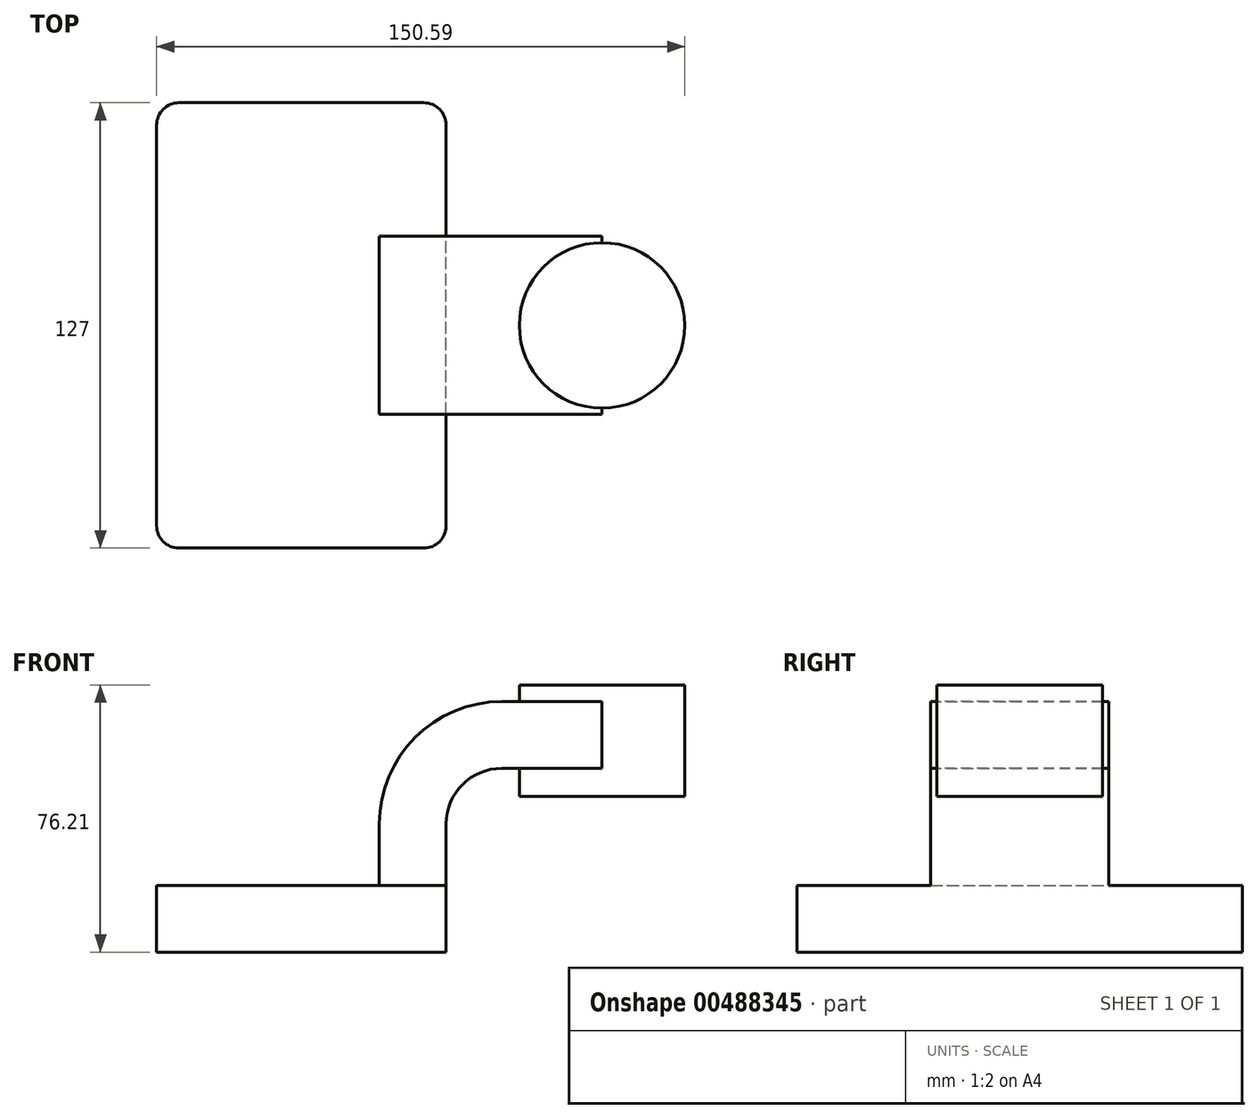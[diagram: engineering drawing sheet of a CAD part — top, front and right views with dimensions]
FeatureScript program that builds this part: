
annotation { "Feature Type Name" : "Feature", "Feature Type Description" : "" }
export const myFeature = defineFeature(function(context is Context, id is Id, definition is map)
    precondition{}
    {
        {
            var Q0;
            Q0=qCreatedBy(makeId("Front.planeOp"),FACE);
            var sketch = newSketch(context, id + "F0", { "sketchPlane" : qUnion([Q0])});
            skLineSegment(sketch, "E0.bottom", {"start": v(41.28, -9.52) * mm, "end": v(-41.28, -9.53) * mm});
            skLineSegment(sketch, "E0.top", {"start": v(41.27, 9.53) * mm, "end": v(-41.28, 9.52) * mm});
            skLineSegment(sketch, "E0.left", {"start": v(41.28, -9.52) * mm, "end": v(41.28, 9.53) * mm});
            skLineSegment(sketch, "E0.right", {"start": v(-41.28, -9.53) * mm, "end": v(-41.28, 9.52) * mm});
            skPoint(sketch, "E0.middle", {"position": v(0, 0) * mm});
            skLineSegment(sketch, "E1.bottom", {"start": v(109.32, 34.93) * mm, "end": v(58.52, 34.93) * mm});
            skLineSegment(sketch, "E1.top", {"start": v(109.32, 66.68) * mm, "end": v(58.52, 66.68) * mm});
            skLineSegment(sketch, "E1.left", {"start": v(109.32, 34.93) * mm, "end": v(109.32, 66.68) * mm});
            skLineSegment(sketch, "E1.right", {"start": v(58.52, 34.93) * mm, "end": v(58.52, 66.68) * mm});
            skPoint(sketch, "E1.middle", {"position": v(83.92, 50.8) * mm});
            skLineSegment(sketch, "E2", {"start": v(41.27, 9.53) * mm, "end": v(41.27, 27) * mm});
            skArc(sketch, "E3", {"start": v(41.28, 27) * mm, "mid": v(45.92, 38.23) * mm, "end": v(57.15, 42.88) * mm});
            skLineSegment(sketch, "E4", {"start": v(57.15, 42.88) * mm, "end": v(85.73, 42.88) * mm});
            skLineSegment(sketch, "E5.0", {"start": v(57.15, 61.93) * mm, "end": v(85.73, 61.93) * mm});
            skArc(sketch, "E5.1", {"start": v(22.23, 27) * mm, "mid": v(32.45, 51.7) * mm, "end": v(57.15, 61.93) * mm});
            skLineSegment(sketch, "E5.2", {"start": v(22.23, 9.53) * mm, "end": v(22.23, 27) * mm});
            skFitSpline(sketch, "E6", {"points": [v(-41.28, 9.52) * mm, v(57.15, 61.93) * mm], "startDerivative": vector(-7.2, 101.27) * mm, "endDerivative": vector(150.2, -4.26) * mm});
            skLineSegment(sketch, "E7", {"start": v(85.73, 34.93) * mm, "end": v(85.73, 66.68) * mm});
            skSolve(sketch);
        }
        {
            var Q0;
            Q0=makeQuery(id+"F0.imprint","IMPRINT",FACE,{"disambiguationData":[TD([[makeQuery(id+"F0.imprint","IMPRINT",EDGE,{"derivedFrom":sQuery(id+"F0.wireOp",EDGE,"E0.bottom")}),-1.0]])]});
            extrude(context, id + "F1", {"entities" : qUnion([Q0]), "endBound" : BoundingType.SYMMETRIC, "depth" : 127 * mm});
        }
        {
            var Q0;
            {var subQ1=sQuery(id+"F0.wireOp",EDGE,"E2");Q0=makeQuery(id+"F0.imprint","IMPRINT",FACE,{"disambiguationData":[TD([[makeQuery(id+"F0.imprint","IMPRINT",EDGE,{"derivedFrom":subQ1}),1.0]])]});}
            var Q1;
            {var subQ0=sQuery(id+"F0.wireOp",EDGE,"E4");var subQ1=sQuery(id+"F0.wireOp",EDGE,"E1.right");var subQ2=makeQuery(id+"F0.imprint","INTERSECT",VERTEX,{"derivedFrom":[subQ1,subQ0]});Q1=makeQuery(id+"F0.imprint","IMPRINT",FACE,{"disambiguationData":[TD([[makeQuery(id+"F0.imprint","IMPRINT",EDGE,{"disambiguationData":[TD([[subQ2,-1.0]])],"derivedFrom":subQ1}),-1.0]])]});}
            extrude(context, id + "F2", {"entities" : qUnion([Q0, Q1]), "operationType" : NewBodyOperationType.ADD, "endBound" : BoundingType.SYMMETRIC, "depth" : 50.8 * mm});
        }
        {
            var Q0;
            Q0=makeQuery(id+"F0.imprint","IMPRINT",FACE,{"disambiguationData":[TD([[makeQuery(id+"F0.imprint","IMPRINT",EDGE,{"derivedFrom":sQuery(id+"F0.wireOp",EDGE,"E5.1")}),1.0]])]});
            extrude(context, id + "F3", {"entities" : qUnion([Q0]), "operationType" : NewBodyOperationType.ADD, "endBound" : BoundingType.SYMMETRIC, "depth" : 15.88 * mm});
        }
        {
            var Q0;
            {var subQ0=sQuery(id+"F0.wireOp",EDGE,"E1.left");Q0=makeQuery(id+"F0.imprint","IMPRINT",FACE,{"disambiguationData":[TD([[makeQuery(id+"F0.imprint","IMPRINT",EDGE,{"derivedFrom":subQ0}),1.0]])]});}
            var Q1;
            Q1=sQuery(id+"F0.wireOp",EDGE,"E7");
            revolve(context, id + "F4", {"operationType" : NewBodyOperationType.ADD, "entities" : qUnion([Q0]), "axis" : qUnion([Q1]), "revolveType" : RevolveType.FULL});
        }
        {
            var Q0;
            Q0=makeQuery(id+"F1.opExtrude","CAP_EDGE",EDGE,{"disambiguationData":[OSD([sQuery(id+"F0.wireOp",EDGE,"E0.right")])],"isStart":false});
            var Q1;
            Q1=makeQuery(id+"F1.opExtrude","CAP_EDGE",EDGE,{"disambiguationData":[OSD([sQuery(id+"F0.wireOp",EDGE,"E0.left")])],"isStart":false});
            var Q2;
            Q2=makeQuery(id+"F1.opExtrude","CAP_EDGE",EDGE,{"disambiguationData":[OSD([sQuery(id+"F0.wireOp",EDGE,"E0.left")])],"isStart":true});
            var Q3;
            Q3=makeQuery(id+"F1.opExtrude","CAP_EDGE",EDGE,{"disambiguationData":[OSD([sQuery(id+"F0.wireOp",EDGE,"E0.right")])],"isStart":true});
            fillet(context, id + "F5", {"entities" : qUnion([Q0, Q1, Q2, Q3]), "radius" : 6.35 * mm, "tangentPropagation" : true, "allowEdgeOverflow" : false});
        }
    });
